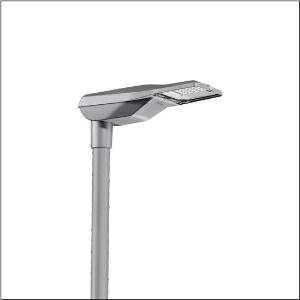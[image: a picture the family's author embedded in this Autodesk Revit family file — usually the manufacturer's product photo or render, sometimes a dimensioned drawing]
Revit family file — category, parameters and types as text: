
# Revit family: streetlight_sl_21_iq_micro___st1_0a_5xe1d41d08db_a30f
name_source: partatom
category: Lighting Fixtures
units: mm (PartAtom-declared; Revit-internal decimal feet)

## family parameters
Cut with Voids When Loaded = No
Host = Face
Light Source = No
Part Type = Normal
Room Calculation Point = No
Round Connector Dimension = Use Diameter
Shared = No

## types (1)
- --- (1 x LED, 5010 lm, 36.4 W, 4000K)
    Apparent Load = 36 VA
    CIE Flux Codes = 37 72 97 100 100
    Color Rendering = 70
    Color Temperature = 4000K
    Default Elevation = 1800 mm
    Description = Streetlight SL 21 iQ micro, mast luminaire, primary light control with lens, of PMMA, primary optical cover: cover, of toughened safety glass, transparent, light distribution: ST1.0a, light emission: direct distribution, primary light characteristic: asymmetric, installation type: post-top, side-entry, LED, High Power LED, rated luminous flux: 5.010lm, luminous efficacy: 138lm/W, light colour: 740, colour temperature: 4000K, control: Auto-Match, Temp-Guard, Lumen-Switch, Night-Set, Smart-Wire, Light-Fading, Desk-Remote (wireless, voltage-free reading and setting of iQ features in the workshop via application-optimized NFC function/RFID function), optimised constant luminous flux control (CLO 2.0), presetting dimming linear, mains connection: 220..240V, AC, 50/60Hz, start of lifetime: 36W, end of service life: 38W, reduction: 16W, luminaire housing, of diecast aluminium, powder-coated, Siteco® metallic grey (DB 702S), corrosivity category C5 mid according to DIN EN ISO 12944, please order mast flange separately, inclination adjustable: 0°, 5°, 10°, 15°, sealing non-destructively replaceable, multi-level sealing system, length: 528mm, width: 235mm, height: 110mm, mast flange for spigot size: 42mm (side-entry): 5XC10008XM4, 60/48mm (side-entry/post-top): 5XC10108XM2, 76/60mm (side-entry/post-top): 5XC10108XM1, protection rating (complete): IP66, insulation class (complete): insulation class II (safety insulation), certification: CE, ENEC, ENEC+, VDE, impact resistance: IK09, permissible operating ambient temperature for outdoor applications: -40..+50°C, standard-compliant lighting for roads and squares, packaging unit: 1 piece

Light Distribution: ST1.0a
    Height = 110 mm
    Lamp = 1 x LED
    Lamp Light Flux = 5010 lm
    Lamp Power = 36.4 W
    Lamp count = 1
    Length = 528 mm
    Luminous efficacy = 138 lm/W
    Manufacturer = Siteco
    ModVariant = No
    Model = 5XE1D41D08DB
    Number of Poles = 1
    OnlyDefault = Yes
    Power Factor = 1
    Product Name = Streetlight SL 21 iQ micro | ST1.0a
    Product group = mast luminaire | pylon top
    ProductGroupID = 6100
    Protection Class = Protection class II
    Protection Degree = IP 66
    RLX_Detail_Level = 1
    RLX_Emergency_Light_Flux = 0 lm
    RLX_Emergency_Type = 0
    RLX_Emergency_Type_DB = No
    RlxData = <blob elided: 99401 chars, md5=cdb65fcf>
    Socket = socket
    Standby Power = 0 W
    System Light Flux = 5010 lm
    System Power = 36 W
    Type Comments = factory setting: luminous flux: 100 % | dim-lin: 254 | 715 mA
    Type Image = l_1006881.jpg
    URL = http://relux.com
    VarID = @adj_106105
    Voltage = 0 V
    Weight = 0.00 kg
    Width = 235 mm

## geometry (parser evidence)
native form markers: Blend x4, Sweep x10
no freeform markers — native parametric forms only
